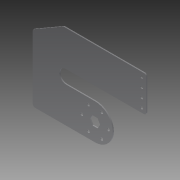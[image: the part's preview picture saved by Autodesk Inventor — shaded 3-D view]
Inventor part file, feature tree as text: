
AUTODESK INVENTOR PART (.ipt)
format: ipt  version: 2014 (Build 180170000, 170)  size: 137,216 bytes
history: native  units: in
note: dims shown in document units (in); Inventor stores cm internally (conversion verified against a paired STEP export)
features: extrude x1, fillet x1
ambient origin geometry x8: Origin, YZ Plane, XZ Plane, XY Plane, X Axis, Y Axis, Z Axis, Center Point
bodies: Solid1 (feature_tree)
feature tree (2):
  extrude  "Extrusion1"  Depth=0.0625in TaperAngle=0.0deg
  fillet  "Fillet1"  Radius=0.625in
